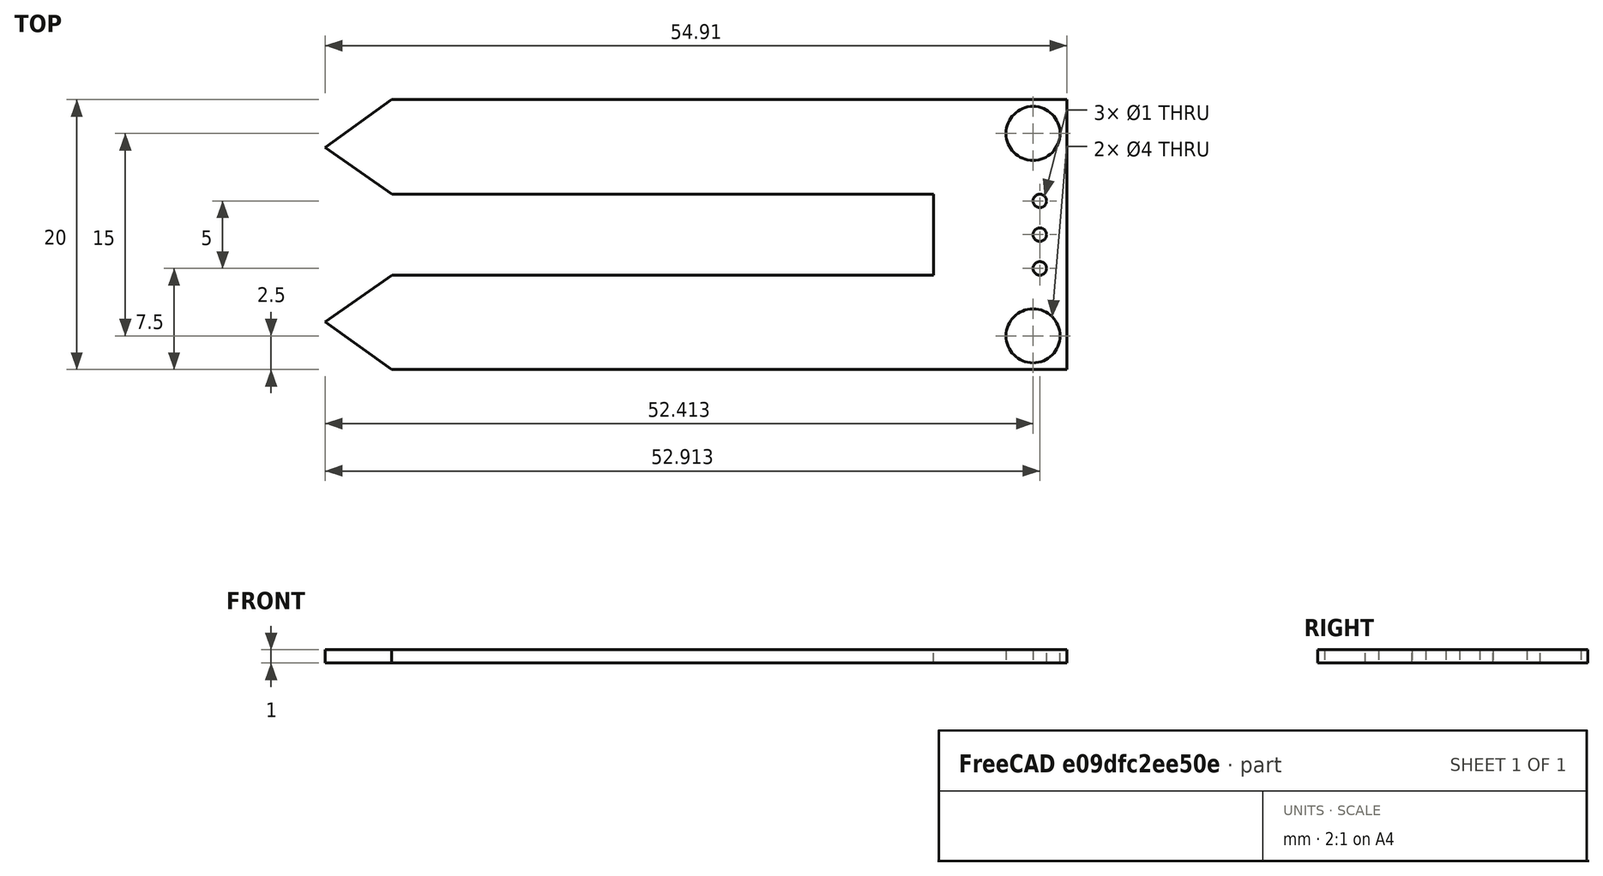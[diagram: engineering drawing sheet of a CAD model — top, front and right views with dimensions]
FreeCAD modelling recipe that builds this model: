
FCSTD DOCUMENT  (FreeCAD 0.17R13522 (Git))
Label: MoistureSensor
License: All rights reserved
LicenseURL: http://en.wikipedia.org/wiki/All_rights_reserved
objects: Sketcher::SketchObject×1, PartDesign::Pad×1
note: 3 computed .brp shape members not serialized (recipe doc carries the construction recipe); baked Part::Feature solids carry a one-line shape summary decoded from their .brp

FEATURE [Sketcher::SketchObject] Sketch
  MapMode = 5
  sketch-geometry (15):
    g0: LineSegment StartX=35.0932 StartY=10 StartZ=0 EndX=35.0932 EndY=-10 EndZ=0
    g1: LineSegment StartX=35.0932 StartY=10 StartZ=0 EndX=-14.9068 EndY=10 EndZ=0
    g2: LineSegment StartX=35.0932 StartY=-10 StartZ=0 EndX=-14.9068 EndY=-10 EndZ=0
    g3: LineSegment StartX=-14.8614 StartY=-3.00015 StartZ=0 EndX=25.2161 EndY=-3.00015 EndZ=0
    g4: LineSegment StartX=25.2161 StartY=3.00015 StartZ=0 EndX=-14.8614 EndY=3.00015 EndZ=0
    g5: LineSegment StartX=-14.8614 StartY=3.00015 StartZ=0 EndX=-19.8197 EndY=6.4681 EndZ=0
    g6: LineSegment StartX=-19.8197 StartY=6.4681 StartZ=0 EndX=-14.9068 EndY=10 EndZ=0
    g7: LineSegment StartX=25.2161 StartY=-3.00015 StartZ=0 EndX=25.2161 EndY=3.00015 EndZ=0
    g8: LineSegment StartX=-14.8614 StartY=-3.00015 StartZ=0 EndX=-19.8197 EndY=-6.4681 EndZ=0
    g9: LineSegment StartX=-19.8197 StartY=-6.4681 StartZ=0 EndX=-14.9068 EndY=-10 EndZ=0
    g10: Circle CenterX=32.5932 CenterY=7.5 CenterZ=0 NormalX=0 NormalY=0 NormalZ=1 AngleXU=0 Radius=2
    g11: Circle CenterX=32.5932 CenterY=-7.5 CenterZ=0 NormalX=0 NormalY=0 NormalZ=1 AngleXU=0 Radius=2
    g12: Circle CenterX=33.0932 CenterY=2.5 CenterZ=0 NormalX=0 NormalY=0 NormalZ=1 AngleXU=0 Radius=0.5
    g13: Circle CenterX=33.0932 CenterY=0 CenterZ=0 NormalX=0 NormalY=0 NormalZ=1 AngleXU=0 Radius=0.5
    g14: Circle CenterX=33.0932 CenterY=-2.5 CenterZ=0 NormalX=0 NormalY=0 NormalZ=1 AngleXU=0 Radius=0.5
  constraints (39):
    c: Vertical(g0)
    c: Coincident(g1,g0)
    c: Coincident(g2,g0)
    c: Horizontal(g2)
    c: Horizontal(g3)
    c: Horizontal(g4)
    c: Coincident(g5,g4)
    c: Coincident(g6,g5)
    c: Coincident(g6,g1)
    c: Distance(g0) = 20
    c: Coincident(g7,g3)
    c: Coincident(g7,g4)
    c: Vertical(g7)
    c: Coincident(g8,g3)
    c: Coincident(g9,g8)
    c: Coincident(g9,g2)
    c: Distance(g2) = 50
    c: Equal(g2,g1)
    c: Parallel(g4,g1)
    c: Equal(g4,g3)
    c: Equal(g9,g8)
    c: Equal(g8,g5)
    c: Equal(g5,g6)
    c: Equal(g11,g10)
    c: Radius(g11) = 2
    c: PointOnObject(g13,g-1)
    c: Equal(g12,g13)
    c: DistanceY(g14,g13) = 2.5
    c: DistanceY(g13,g12) = 2.5
    c: Distance(g13,g0) = 2
    c: Distance(g14,g0) = 2
    c: Distance(g12,g0) = 2
    c: Distance(g11,g2) = 2.5
    c: Distance(g10,g1) = 2.5
    c: Distance(g10,g0) = 2.5
    c: Distance(g11,g0) = 2.5
    c: Distance(g4,g1) = 7
    c: Distance(g2,g3) = 7
    c: Distance(g13,g2) = 10
FEATURE [PartDesign::Pad] Pad
  Length = 1
  Length2 = 100
  Profile = -> Sketch
  Type = 0
